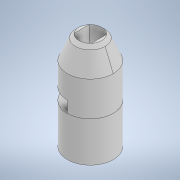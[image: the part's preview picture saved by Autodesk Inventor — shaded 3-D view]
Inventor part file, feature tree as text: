
AUTODESK INVENTOR PART (.ipt)
format: ipt  version: 2020 (Build 240168000, 168)  size: 151,552 bytes
history: native  units: mm
features: extrude x4, sketch x4, chamfer x2
ambient origin geometry x8: Origin, YZ Plane, XZ Plane, XY Plane, X Axis, Y Axis, Z Axis, Center Point
bodies: Solid1 (feature_tree), Solid3 (feature_tree)
feature tree (10):
  extrude  "Extrusion1"  Depth=7.0mm TaperAngle=0.0deg
  extrude  "Extrusion2"  Depth=10.0mm
  extrude  "Extrusion3"  Depth=7.0mm TaperAngle=0.0deg
  chamfer  "Chamfer1"  Distance=2.0mm Angle=45.0deg
  chamfer  "Chamfer2"  Distance=2.0mm Angle=45.0deg
  extrude  "Extrusion4"  Depth=7.0mm TaperAngle=0.0deg
  sketch  "Sketch1"  dims[d0=8.0mm d1=7.0mm d2=0.0mm]
  sketch  "Sketch2"  dims[d3=10.0mm d4=0.0mm d5=3.0mm]
  sketch  "Sketch3"  dims[d6=4.0mm d7=7.0mm d8=0.0mm d9=2.0mm d10=2.0mm d11=45.0deg d12=2.0mm d13=2.0mm d14=45.0deg]
  sketch  "Sketch4"  dims[d15=2.0mm d16=7.0mm d17=0.0mm]
